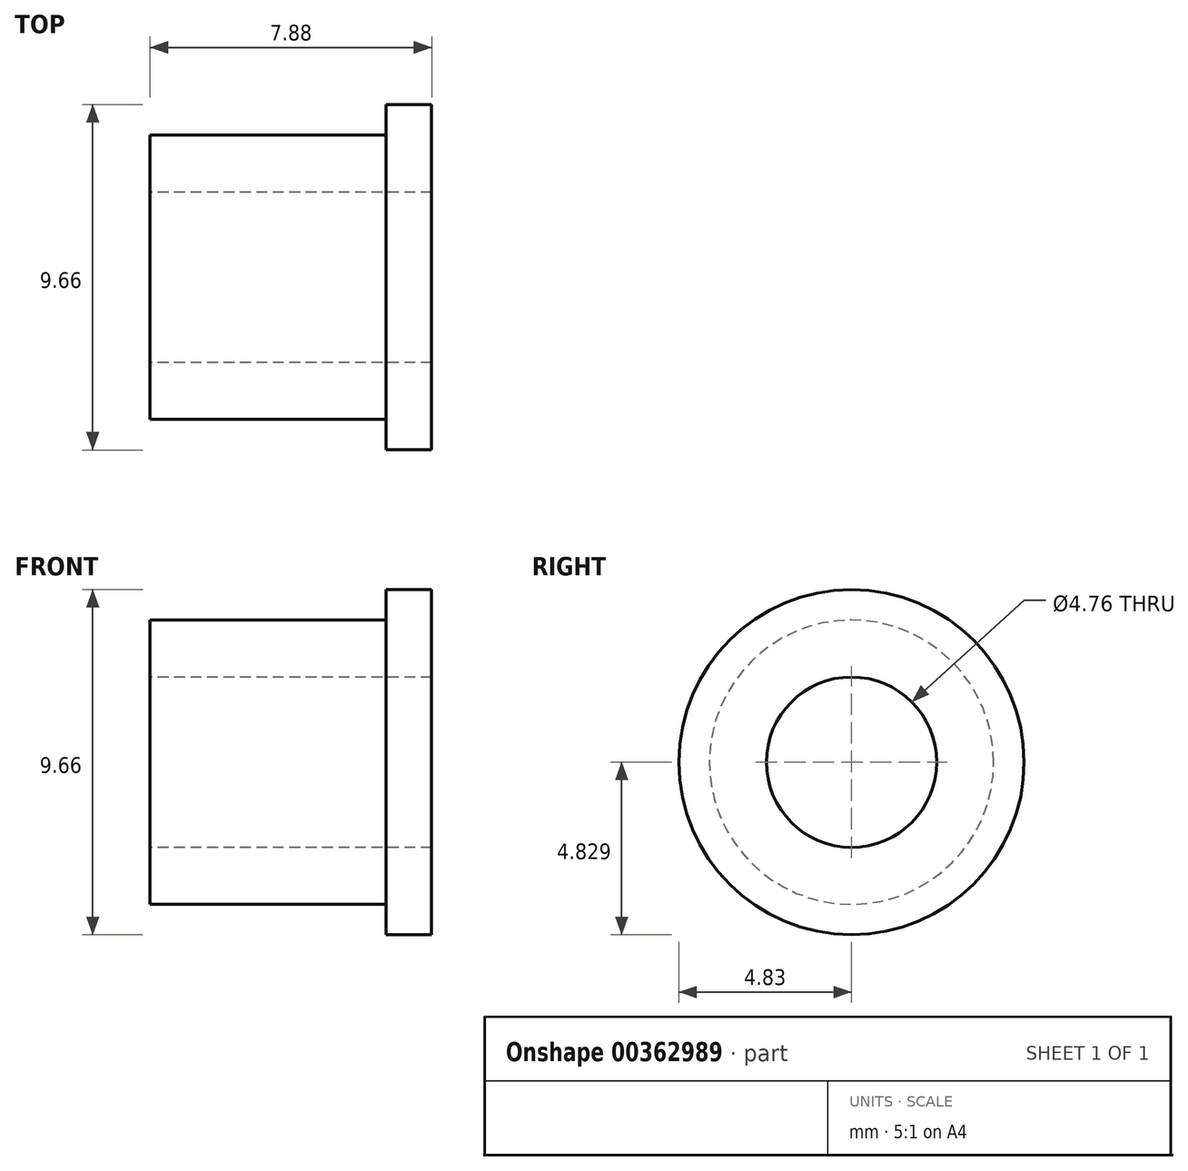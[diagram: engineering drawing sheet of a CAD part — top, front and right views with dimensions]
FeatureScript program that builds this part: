
annotation { "Feature Type Name" : "Feature", "Feature Type Description" : "" }
export const myFeature = defineFeature(function(context is Context, id is Id, definition is map)
    precondition{}
    {
        {
            var Q0;
            Q0=qCreatedBy(makeId("Front.planeOp"),FACE);
            var sketch = newSketch(context, id + "F0", { "sketchPlane" : qUnion([Q0])});
            skLineSegment(sketch, "E0", {"start": v(-32.39, -20.14) * mm, "end": v(-25.78, -20.14) * mm});
            skLineSegment(sketch, "E1", {"start": v(-25.78, -20.14) * mm, "end": v(-25.78, -20.99) * mm});
            skLineSegment(sketch, "E2", {"start": v(-25.78, -20.99) * mm, "end": v(-24.51, -20.99) * mm});
            skLineSegment(sketch, "E3", {"start": v(-24.51, -20.99) * mm, "end": v(-24.51, -18.54) * mm});
            skLineSegment(sketch, "E4", {"start": v(-24.51, -18.54) * mm, "end": v(-32.39, -18.54) * mm});
            skLineSegment(sketch, "E5", {"start": v(-32.39, -18.54) * mm, "end": v(-32.39, -20.14) * mm});
            skLineSegment(sketch, "E6", {"start": v(-34, -16.16) * mm, "end": v(-18.9, -16.16) * mm, "construction": true});
            skSolve(sketch);
        }
        {
            var Q0;
            Q0=makeQuery(id+"F0.imprint","IMPRINT",FACE,{"disambiguationData":[TD([[makeQuery(id+"F0.imprint","IMPRINT",EDGE,{"derivedFrom":sQuery(id+"F0.wireOp",EDGE,"E0")}),1.0]])]});
            var Q1;
            Q1=sQuery(id+"F0.wireOp",EDGE,"E6");
            revolve(context, id + "F1", {"entities" : qUnion([Q0]), "axis" : qUnion([Q1]), "revolveType" : RevolveType.FULL});
        }
    });
